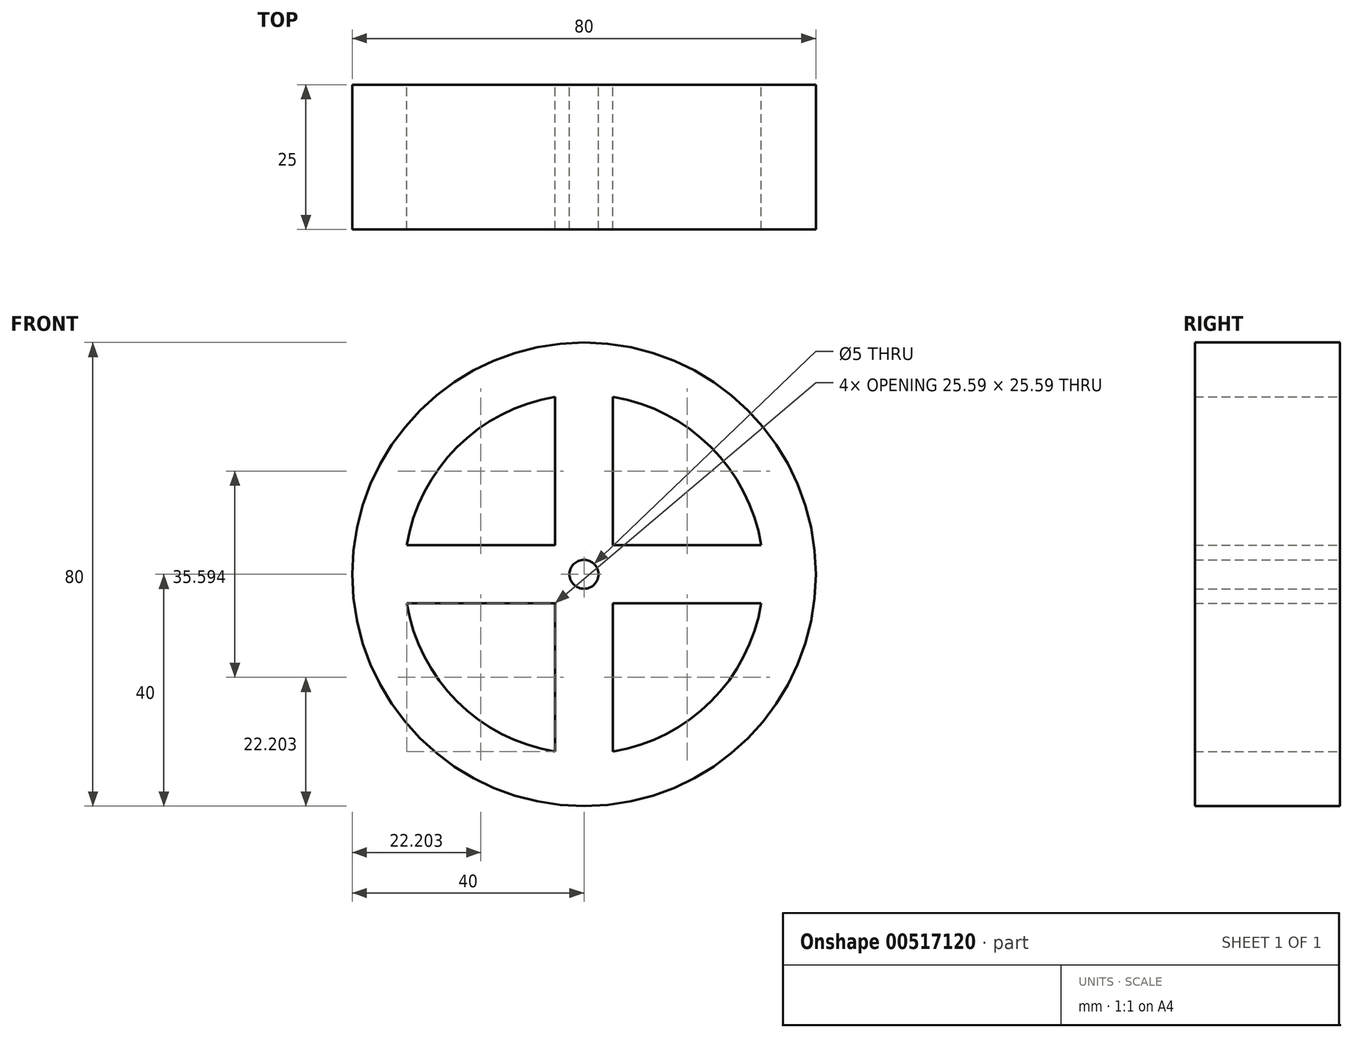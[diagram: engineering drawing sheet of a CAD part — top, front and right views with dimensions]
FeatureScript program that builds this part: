
annotation { "Feature Type Name" : "Feature", "Feature Type Description" : "" }
export const myFeature = defineFeature(function(context is Context, id is Id, definition is map)
    precondition{}
    {
        {
            var Q0;
            Q0=qCreatedBy(makeId("Front.planeOp"),FACE);
            var sketch = newSketch(context, id + "F0", { "sketchPlane" : qUnion([Q0])});
            skCircle(sketch, "E0", {"center": v(0, 0) * mm, "radius": 2.5 * mm});
            skArc(sketch, "E1", {"start": v(-5, 5.6) * mm, "mid": v(-5.3, 5.3) * mm, "end": v(-5.6, 5) * mm});
            skArc(sketch, "E2", {"start": v(30.6, 5) * mm, "mid": v(21.92, 21.92) * mm, "end": v(5, 30.6) * mm});
            skCircle(sketch, "E3", {"center": v(0, 0) * mm, "radius": 40 * mm});
            skLineSegment(sketch, "E4", {"start": v(-2.5, 0) * mm, "end": v(-7.5, 0) * mm});
            skLineSegment(sketch, "E5", {"start": v(0, 2.5) * mm, "end": v(0, 5) * mm});
            skLineSegment(sketch, "E6", {"start": v(0, 0) * mm, "end": v(0, -2.5) * mm});
            skLineSegment(sketch, "E7.0", {"start": v(5, 5) * mm, "end": v(5, 30.6) * mm});
            skLineSegment(sketch, "E8.0", {"start": v(-5, 5) * mm, "end": v(-5, 30.6) * mm});
            skLineSegment(sketch, "E9.0", {"start": v(-5, -5) * mm, "end": v(-30.6, -5) * mm});
            skLineSegment(sketch, "E10.0", {"start": v(-5, 5) * mm, "end": v(-30.6, 5) * mm});
            skLineSegment(sketch, "E11.0", {"start": v(-5, -5) * mm, "end": v(-5, -30.6) * mm});
            skLineSegment(sketch, "E12.0", {"start": v(5, -5) * mm, "end": v(5, -30.6) * mm});
            skLineSegment(sketch, "E13.0", {"start": v(5, -5) * mm, "end": v(30.6, -5) * mm});
            skLineSegment(sketch, "E14.0", {"start": v(5, 5) * mm, "end": v(30.6, 5) * mm});
            skArc(sketch, "E15.trimOffspring", {"start": v(5, -30.6) * mm, "mid": v(21.92, -21.92) * mm, "end": v(30.6, -5) * mm});
            skArc(sketch, "E16.trimOffspring", {"start": v(-30.6, -5) * mm, "mid": v(-21.92, -21.92) * mm, "end": v(-5, -30.6) * mm});
            skArc(sketch, "E17.trimOffspring", {"start": v(-5, 30.6) * mm, "mid": v(-21.92, 21.92) * mm, "end": v(-30.6, 5) * mm});
            skArc(sketch, "E18.trimOffspring", {"start": v(5, -5.6) * mm, "mid": v(5.3, -5.3) * mm, "end": v(5.6, -5) * mm});
            skArc(sketch, "E19.trimOffspring", {"start": v(5.6, 5) * mm, "mid": v(5.3, 5.3) * mm, "end": v(5, 5.6) * mm});
            skLineSegment(sketch, "E20.trimOffspring", {"start": v(-5, 39.69) * mm, "end": v(-5, 40) * mm});
            skLineSegment(sketch, "E21.trimOffspring", {"start": v(5, 39.69) * mm, "end": v(5, 40) * mm});
            skLineSegment(sketch, "E22.trimOffspring", {"start": v(39.69, -5) * mm, "end": v(40, -5) * mm});
            skLineSegment(sketch, "E23.trimOffspring", {"start": v(39.69, 5) * mm, "end": v(40, 5) * mm});
            skLineSegment(sketch, "E24.trimOffspring", {"start": v(-39.69, 5) * mm, "end": v(-40, 5) * mm});
            skLineSegment(sketch, "E25.trimOffspring", {"start": v(-39.69, -5) * mm, "end": v(-40, -5) * mm});
            skLineSegment(sketch, "E26.trimOffspring", {"start": v(-5, -39.69) * mm, "end": v(-5, -40) * mm});
            skLineSegment(sketch, "E27.trimOffspring", {"start": v(5, -39.69) * mm, "end": v(5, -40) * mm});
            skSolve(sketch);
        }
        {
            var Q0;
            {var subQ14=sQuery(id+"F0.wireOp",EDGE,"E2");Q0=makeQuery(id+"F0.imprint","IMPRINT",FACE,{"disambiguationData":[TD([[makeQuery(id+"F0.imprint","IMPRINT",EDGE,{"derivedFrom":subQ14}),-1.0]])]});}
            var Q1;
            Q1 = qSketchRegion(id + "F0", true);
            extrude(context, id + "F1", {"entities" : qUnion([Q0, Q1]), "depth" : 25 * mm, "offsetDistance" : 25 * mm});
        }
    });
